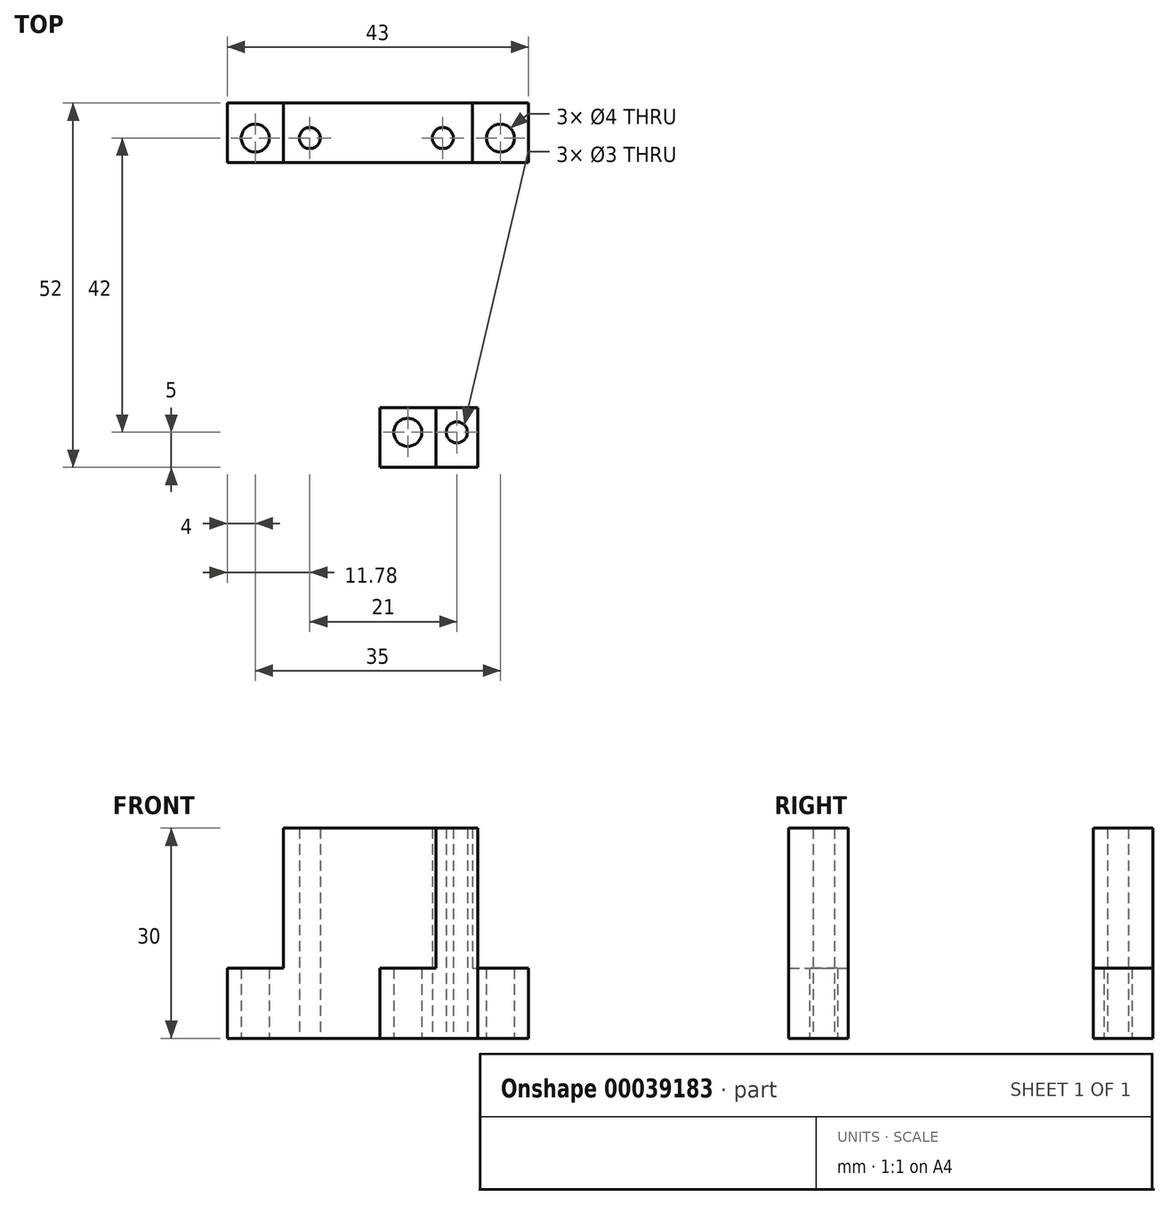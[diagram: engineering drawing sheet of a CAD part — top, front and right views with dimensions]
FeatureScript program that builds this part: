
annotation { "Feature Type Name" : "Feature", "Feature Type Description" : "" }
export const myFeature = defineFeature(function(context is Context, id is Id, definition is map)
    precondition{}
    {
        {
            var Q0;
            Q0=qCreatedBy(makeId("Top.planeOp"),FACE);
            var sketch = newSketch(context, id + "F0", { "sketchPlane" : qUnion([Q0])});
            skLineSegment(sketch, "E0", {"start": v(-74.95, 0) * mm, "end": v(83.6, 0) * mm, "construction": true});
            skLineSegment(sketch, "E1", {"start": v(-71.3, 21) * mm, "end": v(76.91, 21) * mm, "construction": true});
            skLineSegment(sketch, "E2.MirrorCS", {"start": v(-71.3, -21) * mm, "end": v(76.91, -21) * mm, "construction": true});
            skLineSegment(sketch, "E3", {"start": v(0, 41.64) * mm, "end": v(0, -58.44) * mm, "construction": true});
            skLineSegment(sketch, "E4", {"start": v(13.22, 41.98) * mm, "end": v(13.22, -40.9) * mm, "construction": true});
            skCircle(sketch, "E5", {"center": v(0, -21) * mm, "radius": 2 * mm});
            skLineSegment(sketch, "E6", {"start": v(-21.78, 41.89) * mm, "end": v(-21.78, -41.17) * mm, "construction": true});
            skCircle(sketch, "E7", {"center": v(13.22, 21) * mm, "radius": 2 * mm});
            skCircle(sketch, "E8", {"center": v(-21.78, 21) * mm, "radius": 2 * mm});
            skLineSegment(sketch, "E9", {"start": v(-25.78, 17.5) * mm, "end": v(17.22, 17.5) * mm});
            skLineSegment(sketch, "E10.MirrorCS", {"start": v(-4, -17.5) * mm, "end": v(10, -17.5) * mm});
            skLineSegment(sketch, "E11", {"start": v(-25.78, 26) * mm, "end": v(17.22, 26) * mm});
            skLineSegment(sketch, "E12.MirrorCS", {"start": v(-4, -26) * mm, "end": v(10, -26) * mm});
            skLineSegment(sketch, "E13", {"start": v(17.22, 26) * mm, "end": v(17.22, 17.5) * mm});
            skLineSegment(sketch, "E14", {"start": v(-25.78, 26) * mm, "end": v(-25.78, 17.5) * mm});
            skLineSegment(sketch, "E15", {"start": v(-4, -17.5) * mm, "end": v(-4, -26) * mm});
            skPoint(sketch, "E16.orphan", {"position": v(-40.59, 26) * mm});
            skPoint(sketch, "E17.orphan", {"position": v(-39.93, 17.5) * mm});
            skPoint(sketch, "E18.orphan", {"position": v(26.23, 26) * mm});
            skPoint(sketch, "E19.orphan", {"position": v(27.44, 17.5) * mm});
            skPoint(sketch, "E20.orphan", {"position": v(-39.93, -17.5) * mm});
            skPoint(sketch, "E21.orphan", {"position": v(-40.59, -26) * mm});
            skLineSegment(sketch, "E22", {"start": v(10, -17.5) * mm, "end": v(10, -26) * mm});
            skPoint(sketch, "E23.orphan", {"position": v(27.44, -17.5) * mm});
            skPoint(sketch, "E24.orphan", {"position": v(26.23, -26) * mm});
            skLineSegment(sketch, "E25", {"start": v(4, -17.5) * mm, "end": v(4, -26) * mm});
            skLineSegment(sketch, "E26", {"start": v(9.22, 26) * mm, "end": v(9.22, 17.5) * mm});
            skLineSegment(sketch, "E27", {"start": v(-17.78, 26) * mm, "end": v(-17.78, 17.5) * mm});
            skLineSegment(sketch, "E28", {"start": v(7, -13.7) * mm, "end": v(7, -30.15) * mm, "construction": true});
            skLineSegment(sketch, "E29", {"start": v(5, 30.35) * mm, "end": v(5, 7.13) * mm, "construction": true});
            skLineSegment(sketch, "E30", {"start": v(-14, 29.78) * mm, "end": v(-14, 11.95) * mm, "construction": true});
            skPoint(sketch, "E31", {"position": v(5, 21) * mm});
            skPoint(sketch, "E32", {"position": v(7, -21) * mm});
            skPoint(sketch, "E33", {"position": v(-14, 21) * mm});
            skCircle(sketch, "E34", {"center": v(-14, 21) * mm, "radius": 1.5 * mm});
            skCircle(sketch, "E35", {"center": v(5, 21) * mm, "radius": 1.5 * mm});
            skCircle(sketch, "E36", {"center": v(7, -21) * mm, "radius": 1.5 * mm});
            skSolve(sketch);
        }
        {
            var Q0;
            Q0=makeQuery(id+"F0.imprint","IMPRINT",FACE,{"disambiguationData":[TD([[makeQuery(id+"F0.imprint","IMPRINT",EDGE,{"derivedFrom":sQuery(id+"F0.wireOp",EDGE,"E8")}),-1.0]])]});
            var Q1;
            {var subQ2=sQuery(id+"F0.wireOp",EDGE,"E26");Q1=makeQuery(id+"F0.imprint","IMPRINT",FACE,{"disambiguationData":[TD([[makeQuery(id+"F0.imprint","IMPRINT",EDGE,{"derivedFrom":subQ2}),-1.0]])]});}
            var Q2;
            Q2=makeQuery(id+"F0.imprint","IMPRINT",FACE,{"disambiguationData":[TD([[makeQuery(id+"F0.imprint","IMPRINT",EDGE,{"derivedFrom":sQuery(id+"F0.wireOp",EDGE,"E7")}),-1.0]])]});
            extrude(context, id + "F1", {"entities" : qUnion([Q0, Q1, Q2]), "depth" : 10 * mm});
        }
        {
            var Q0;
            {var subQ2=sQuery(id+"F0.wireOp",EDGE,"E26");Q0=makeQuery(id+"F0.imprint","IMPRINT",FACE,{"disambiguationData":[TD([[makeQuery(id+"F0.imprint","IMPRINT",EDGE,{"derivedFrom":subQ2}),-1.0]])]});}
            extrude(context, id + "F2", {"entities" : qUnion([Q0]), "operationType" : NewBodyOperationType.ADD, "depth" : 30 * mm});
        }
        {
            var Q0;
            Q0=makeQuery(id+"F0.imprint","IMPRINT",FACE,{"disambiguationData":[TD([[makeQuery(id+"F0.imprint","IMPRINT",EDGE,{"derivedFrom":sQuery(id+"F0.wireOp",EDGE,"E5")}),-1.0]])]});
            var Q1;
            {var subQ2=sQuery(id+"F0.wireOp",EDGE,"E22");Q1=makeQuery(id+"F0.imprint","IMPRINT",FACE,{"disambiguationData":[TD([[makeQuery(id+"F0.imprint","IMPRINT",EDGE,{"derivedFrom":subQ2}),-1.0]])]});}
            extrude(context, id + "F3", {"entities" : qUnion([Q0, Q1]), "depth" : 10 * mm});
        }
        {
            var Q0;
            {var subQ2=sQuery(id+"F0.wireOp",EDGE,"E22");Q0=makeQuery(id+"F0.imprint","IMPRINT",FACE,{"disambiguationData":[TD([[makeQuery(id+"F0.imprint","IMPRINT",EDGE,{"derivedFrom":subQ2}),-1.0]])]});}
            extrude(context, id + "F4", {"entities" : qUnion([Q0]), "operationType" : NewBodyOperationType.ADD, "depth" : 30 * mm});
        }
    });
